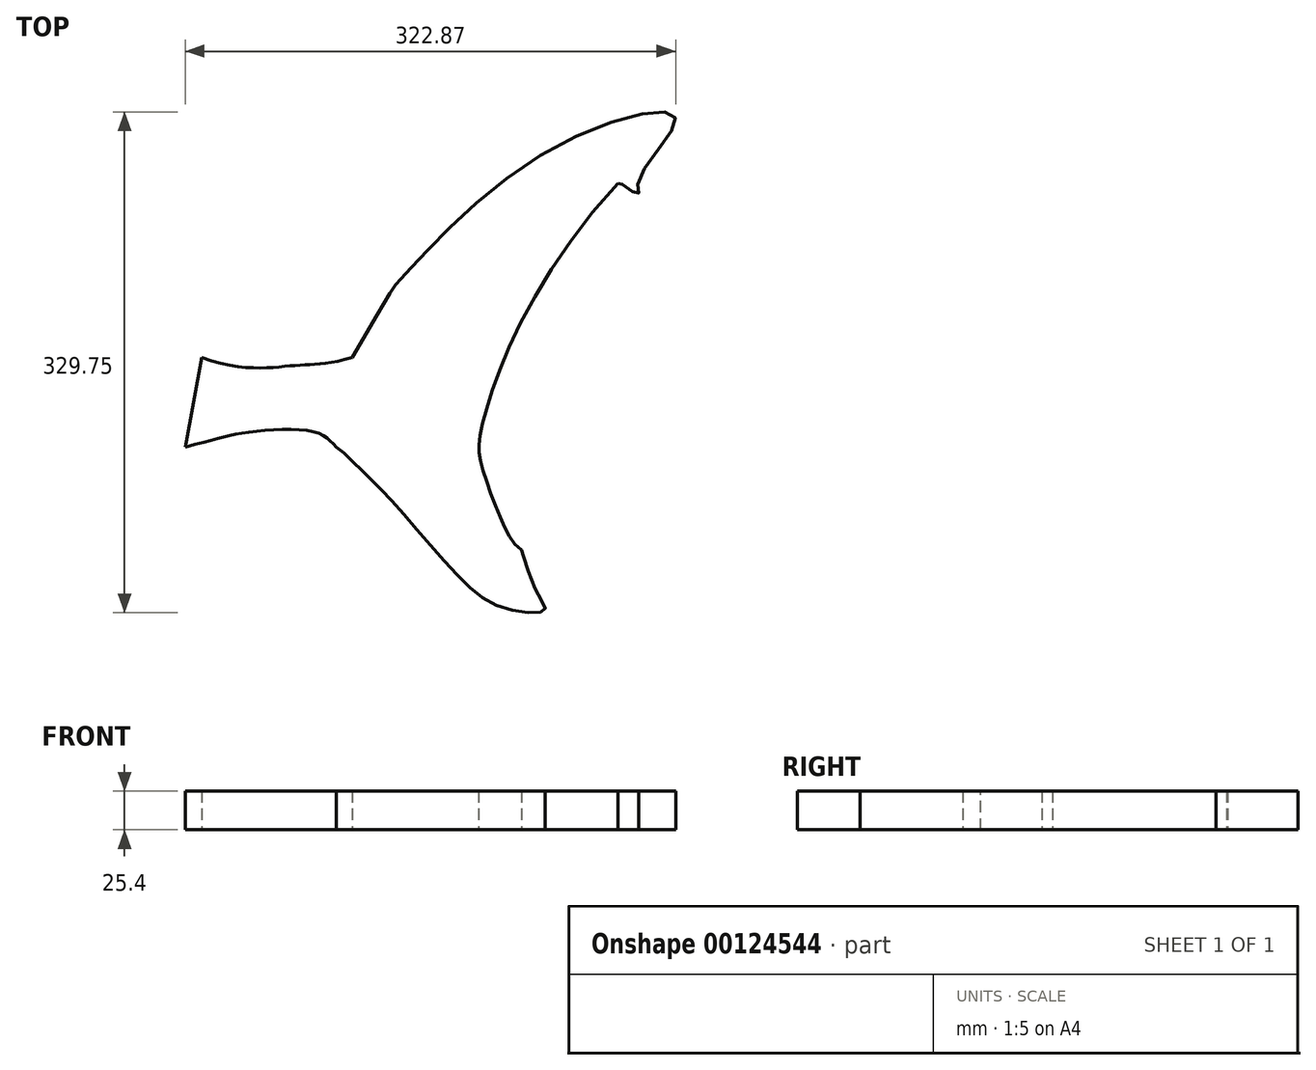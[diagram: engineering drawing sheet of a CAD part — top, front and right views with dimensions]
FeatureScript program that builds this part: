
annotation { "Feature Type Name" : "Feature", "Feature Type Description" : "" }
export const myFeature = defineFeature(function(context is Context, id is Id, definition is map)
    precondition{}
    {
        {
            var Q0;
            Q0=qCreatedBy(makeId("Top.planeOp"),FACE);
            var sketch = newSketch(context, id + "F0", { "sketchPlane" : qUnion([Q0])});
            skFitSpline(sketch, "E0", {"points": [v(763.03, -9.39) * mm, v(778.15, -23.41) * mm, v(799.33, -44.6) * mm, v(839.5, -90.53) * mm, v(873.7, -115.53) * mm, v(900.01, -116.85) * mm, v(894.73, -104.78) * mm, v(884.95, -77.16) * mm], "startDerivative": vector(95.54, -64.8) * mm, "endDerivative": vector(0, -10.36) * mm});
            skFitSpline(sketch, "E1", {"points": [v(884.95, -77.16) * mm, v(870.9, -55.67) * mm, v(857.92, -19.21) * mm, v(857.92, 0) * mm, v(948.2, 164.28) * mm], "startDerivative": vector(-114.99, 76.84) * mm, "endDerivative": vector(405.42, 441.45) * mm});
            skFitSpline(sketch, "E2", {"points": [v(948.2, 164.28) * mm, v(950.16, 164.28) * mm, v(961.48, 157.26) * mm, v(961.48, 164.91) * mm, v(986.28, 206.44) * mm, v(900.6, 184.6) * mm, v(806.43, 102.16) * mm, v(773.3, 49.59) * mm], "startDerivative": vector(136.84, 88.5) * mm, "endDerivative": vector(-506.85, -865.24) * mm});
            skFitSpline(sketch, "E3", {"points": [v(773.3, 49.59) * mm, v(735.21, 44.25) * mm, v(674.16, 49.59) * mm], "startDerivative": vector(-120.6, -36.08) * mm, "endDerivative": vector(-154.68, 55.08) * mm});
            skFitSpline(sketch, "E4", {"points": [v(763.03, -9.39) * mm, v(750.5, 0) * mm, v(702.92, 0) * mm, v(663.44, -9.39) * mm], "startDerivative": vector(-54.33, 46.93) * mm, "endDerivative": vector(-162.73, -41.26) * mm});
            skLineSegment(sketch, "E5", {"start": v(674.16, 49.59) * mm, "end": v(663.44, -9.39) * mm});
            skSolve(sketch);
        }
        {
            var Q0;
            Q0=makeQuery(id+"F0.imprint","IMPRINT",FACE,{"disambiguationData":[TD([[makeQuery(id+"F0.imprint","IMPRINT",EDGE,{"derivedFrom":sQuery(id+"F0.wireOp",EDGE,"E0")}),1.0]])]});
            extrude(context, id + "F1", {"entities" : qUnion([Q0]), "depth" : 25.4 * mm});
        }
    });
